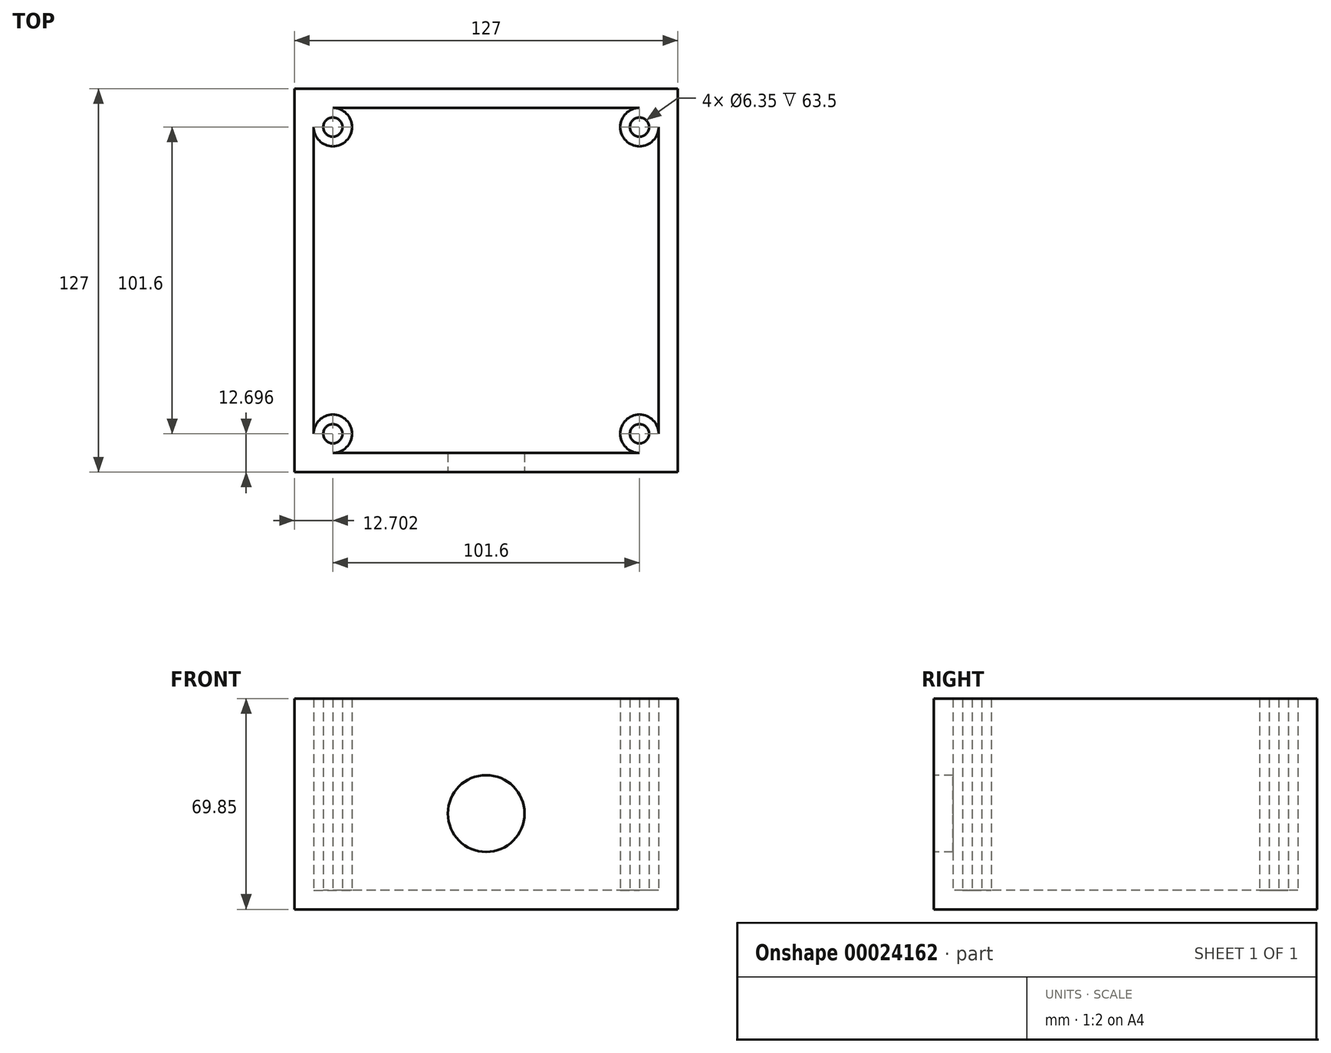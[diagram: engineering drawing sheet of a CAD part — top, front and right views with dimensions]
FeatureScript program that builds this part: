
annotation { "Feature Type Name" : "Feature", "Feature Type Description" : "" }
export const myFeature = defineFeature(function(context is Context, id is Id, definition is map)
    precondition{}
    {
        {
            var Q0;
            Q0=qCreatedBy(makeId("Top.planeOp"),FACE);
            var sketch = newSketch(context, id + "F0", { "sketchPlane" : qUnion([Q0])});
            skLineSegment(sketch, "E0.bottom", {"start": v(-155.82, 63.15) * mm, "end": v(-28.82, 63.15) * mm});
            skLineSegment(sketch, "E0.top", {"start": v(-155.82, -63.85) * mm, "end": v(-28.82, -63.85) * mm});
            skLineSegment(sketch, "E0.left", {"start": v(-155.82, 63.15) * mm, "end": v(-155.82, -63.85) * mm});
            skLineSegment(sketch, "E0.right", {"start": v(-28.82, 63.15) * mm, "end": v(-28.82, -63.85) * mm});
            skSolve(sketch);
        }
        {
            var Q0;
            Q0=makeQuery(id+"F0.imprint","IMPRINT",FACE,{"disambiguationData":[TD([[makeQuery(id+"F0.imprint","IMPRINT",EDGE,{"derivedFrom":sQuery(id+"F0.wireOp",EDGE,"E0.bottom")}),-1.0]])]});
            extrude(context, id + "F1", {"entities" : qUnion([Q0]), "depth" : 6.35 * mm});
        }
        {
            var Q0;
            Q0=makeQuery(id+"F1.opExtrude","CAP_FACE",FACE,{"disambiguationData":[OSD([sQuery(id+"F0.wireOp",EDGE,"E0.bottom"),sQuery(id+"F0.wireOp",EDGE,"E0.top"),sQuery(id+"F0.wireOp",EDGE,"E0.left"),sQuery(id+"F0.wireOp",EDGE,"E0.right")])],"isStart":false});
            var sketch = newSketch(context, id + "F2", { "sketchPlane" : qUnion([Q0])});
            skLineSegment(sketch, "E1.bottom", {"start": v(-155.82, -63.85) * mm, "end": v(-149.47, -63.85) * mm});
            skLineSegment(sketch, "E1.top", {"start": v(-155.82, 63.15) * mm, "end": v(-149.47, 63.15) * mm});
            skLineSegment(sketch, "E1.left", {"start": v(-155.82, -63.85) * mm, "end": v(-155.82, 63.15) * mm});
            skLineSegment(sketch, "E1.right", {"start": v(-149.47, -63.85) * mm, "end": v(-149.47, 63.15) * mm});
            skLineSegment(sketch, "E2.bottom", {"start": v(-155.82, 63.15) * mm, "end": v(-28.82, 63.15) * mm});
            skLineSegment(sketch, "E2.top", {"start": v(-155.82, 56.8) * mm, "end": v(-28.82, 56.8) * mm});
            skLineSegment(sketch, "E2.left", {"start": v(-155.82, 63.15) * mm, "end": v(-155.82, 56.8) * mm});
            skLineSegment(sketch, "E2.right", {"start": v(-28.82, 63.15) * mm, "end": v(-28.82, 56.8) * mm});
            skLineSegment(sketch, "E3.bottom", {"start": v(-28.82, 63.15) * mm, "end": v(-35.17, 63.15) * mm});
            skLineSegment(sketch, "E3.top", {"start": v(-28.82, -63.85) * mm, "end": v(-35.17, -63.85) * mm});
            skLineSegment(sketch, "E3.left", {"start": v(-28.82, 63.15) * mm, "end": v(-28.82, -63.85) * mm});
            skLineSegment(sketch, "E3.right", {"start": v(-35.17, 63.15) * mm, "end": v(-35.17, -63.85) * mm});
            skLineSegment(sketch, "E4.bottom", {"start": v(-28.82, -63.85) * mm, "end": v(-155.82, -63.85) * mm});
            skLineSegment(sketch, "E4.top", {"start": v(-28.82, -57.5) * mm, "end": v(-155.82, -57.5) * mm});
            skLineSegment(sketch, "E4.left", {"start": v(-28.82, -63.85) * mm, "end": v(-28.82, -57.5) * mm});
            skLineSegment(sketch, "E4.right", {"start": v(-155.82, -63.85) * mm, "end": v(-155.82, -57.5) * mm});
            skSolve(sketch);
        }
        {
            var Q0;
            Q0 = qSketchRegion(id + "F2", true);
            extrude(context, id + "F3", {"entities" : qUnion([Q0]), "operationType" : NewBodyOperationType.ADD, "depth" : 63.5 * mm});
        }
        {
            var Q0;
            Q0=makeQuery(id+"F3.boolean.opBoolean","MERGE",FACE,{"derivedFrom":[makeQuery(id+"F1.opExtrude","SWEPT_FACE",FACE,{"disambiguationData":[OSD([sQuery(id+"F0.wireOp",EDGE,"E0.top")])]}),makeQuery(id+"F3.opExtrude","SWEPT_FACE",FACE,{"disambiguationData":[OSD([sQuery(id+"F2.wireOp",EDGE,"E4.bottom")])]})]});
            var sketch = newSketch(context, id + "F4", { "sketchPlane" : qUnion([Q0])});
            skCircle(sketch, "E5", {"center": v(-92.32, 31.75) * mm, "radius": 12.7 * mm});
            skSolve(sketch);
        }
        {
            var Q0;
            Q0 = qSketchRegion(id + "F4", true);
            extrude(context, id + "F5", {"entities" : qUnion([Q0]), "operationType" : NewBodyOperationType.REMOVE, "oppositeDirection" : true, "depth" : 25.4 * mm});
        }
        {
            var Q0;
            Q0=makeQuery(id+"F1.opExtrude","CAP_FACE",FACE,{"disambiguationData":[OSD([sQuery(id+"F0.wireOp",EDGE,"E0.bottom"),sQuery(id+"F0.wireOp",EDGE,"E0.top"),sQuery(id+"F0.wireOp",EDGE,"E0.left"),sQuery(id+"F0.wireOp",EDGE,"E0.right")])],"isStart":false});
            var sketch = newSketch(context, id + "F6", { "sketchPlane" : qUnion([Q0])});
            skCircle(sketch, "E6", {"center": v(-143.12, 50.45) * mm, "radius": 6.35 * mm});
            skCircle(sketch, "E7", {"center": v(-143.12, 50.45) * mm, "radius": 3.18 * mm});
            skSolve(sketch);
        }
        {
            var Q0;
            Q0 = qSketchRegion(id + "F6", true);
            var Q1;
            {var subQ1=sQuery(id+"F6.wireOp",EDGE,"E6");var subQ3=makeQuery(id+"F3.opExtrude","CAP_EDGE",EDGE,{"disambiguationData":[OSD([sQuery(id+"F2.wireOp",EDGE,"E1.right")])],"isStart":true});var subQ5=makeQuery(id+"F6.imprint","INTERSECT",VERTEX,{"derivedFrom":[subQ3,subQ1]});Q1=makeQuery(id+"F6.imprint","IMPRINT",FACE,{"disambiguationData":[TD([[makeQuery(id+"F6.imprint","IMPRINT",EDGE,{"disambiguationData":[TD([[subQ5,1.0]])],"derivedFrom":subQ1}),-1.0]])]});}
            extrude(context, id + "F7", {"entities" : qUnion([Q0, Q1]), "operationType" : NewBodyOperationType.ADD, "depth" : 63.5 * mm});
        }
        {
            var Q0;
            Q0=makeQuery(id+"F7.boolean.opBoolean","SPLIT",FACE,{"disambiguationData":[TD([makeQuery(id+"F3.opExtrude","SWEPT_FACE",FACE,{"disambiguationData":[OSD([sQuery(id+"F2.wireOp",EDGE,"E1.right")])]})])],"derivedFrom":makeQuery(id+"F1.opExtrude","CAP_FACE",FACE,{"disambiguationData":[OSD([sQuery(id+"F0.wireOp",EDGE,"E0.bottom"),sQuery(id+"F0.wireOp",EDGE,"E0.top"),sQuery(id+"F0.wireOp",EDGE,"E0.left"),sQuery(id+"F0.wireOp",EDGE,"E0.right")])],"isStart":false})});
            var sketch = newSketch(context, id + "F8", { "sketchPlane" : qUnion([Q0])});
            skCircle(sketch, "E8", {"center": v(-41.52, 50.45) * mm, "radius": 3.18 * mm});
            skCircle(sketch, "E9", {"center": v(-41.52, 50.45) * mm, "radius": 6.35 * mm});
            skSolve(sketch);
        }
        {
            var Q0;
            Q0=makeQuery(id+"F8.imprint","IMPRINT",FACE,{"disambiguationData":[TD([[makeQuery(id+"F8.imprint","IMPRINT",EDGE,{"derivedFrom":sQuery(id+"F8.wireOp",EDGE,"E8")}),-1.0]])]});
            var Q1;
            {var subQ1=sQuery(id+"F8.wireOp",EDGE,"E9");var subQ3=makeQuery(id+"F3.opExtrude","CAP_EDGE",EDGE,{"disambiguationData":[OSD([sQuery(id+"F2.wireOp",EDGE,"E3.right")])],"isStart":true});var subQ5=makeQuery(id+"F8.imprint","INTERSECT",VERTEX,{"derivedFrom":[subQ3,subQ1]});Q1=makeQuery(id+"F8.imprint","IMPRINT",FACE,{"disambiguationData":[TD([[makeQuery(id+"F8.imprint","IMPRINT",EDGE,{"disambiguationData":[TD([[subQ5,-1.0]])],"derivedFrom":subQ1}),-1.0]])]});}
            extrude(context, id + "F9", {"entities" : qUnion([Q0, Q1]), "operationType" : NewBodyOperationType.ADD, "depth" : 63.5 * mm});
        }
        {
            var Q0;
            {var subQ4=makeQuery(id+"F3.opExtrude","SWEPT_FACE",FACE,{"disambiguationData":[OSD([sQuery(id+"F2.wireOp",EDGE,"E1.right")])]});Q0=makeQuery(id+"F9.boolean.opBoolean","SPLIT",FACE,{"disambiguationData":[TD([subQ4])],"derivedFrom":makeQuery(id+"F7.boolean.opBoolean","SPLIT",FACE,{"disambiguationData":[TD([subQ4])],"derivedFrom":makeQuery(id+"F1.opExtrude","CAP_FACE",FACE,{"disambiguationData":[OSD([sQuery(id+"F0.wireOp",EDGE,"E0.bottom"),sQuery(id+"F0.wireOp",EDGE,"E0.top"),sQuery(id+"F0.wireOp",EDGE,"E0.left"),sQuery(id+"F0.wireOp",EDGE,"E0.right")])],"isStart":false})})});}
            var sketch = newSketch(context, id + "F10", { "sketchPlane" : qUnion([Q0])});
            skCircle(sketch, "E10", {"center": v(-143.12, -51.15) * mm, "radius": 6.35 * mm});
            skCircle(sketch, "E11", {"center": v(-143.12, -51.15) * mm, "radius": 3.18 * mm});
            skCircle(sketch, "E12", {"center": v(-41.52, -51.15) * mm, "radius": 6.35 * mm});
            skCircle(sketch, "E13", {"center": v(-41.52, -51.15) * mm, "radius": 3.18 * mm});
            skSolve(sketch);
        }
        {
            var Q0;
            Q0=makeQuery(id+"F10.imprint","IMPRINT",FACE,{"disambiguationData":[TD([[makeQuery(id+"F10.imprint","IMPRINT",EDGE,{"derivedFrom":sQuery(id+"F10.wireOp",EDGE,"E11")}),-1.0]])]});
            var Q1;
            {var subQ1=sQuery(id+"F10.wireOp",EDGE,"E10");var subQ3=makeQuery(id+"F3.opExtrude","CAP_EDGE",EDGE,{"disambiguationData":[OSD([sQuery(id+"F2.wireOp",EDGE,"E4.top")])],"isStart":true});var subQ5=makeQuery(id+"F10.imprint","INTERSECT",VERTEX,{"derivedFrom":[subQ3,subQ1]});Q1=makeQuery(id+"F10.imprint","IMPRINT",FACE,{"disambiguationData":[TD([[makeQuery(id+"F10.imprint","IMPRINT",EDGE,{"disambiguationData":[TD([[subQ5,1.0]])],"derivedFrom":subQ1}),-1.0]])]});}
            var Q2;
            Q2=makeQuery(id+"F10.imprint","IMPRINT",FACE,{"disambiguationData":[TD([[makeQuery(id+"F10.imprint","IMPRINT",EDGE,{"derivedFrom":sQuery(id+"F10.wireOp",EDGE,"E13")}),-1.0]])]});
            var Q3;
            {var subQ1=sQuery(id+"F10.wireOp",EDGE,"E12");var subQ3=makeQuery(id+"F3.opExtrude","CAP_EDGE",EDGE,{"disambiguationData":[OSD([sQuery(id+"F2.wireOp",EDGE,"E4.top")])],"isStart":true});var subQ5=makeQuery(id+"F10.imprint","INTERSECT",VERTEX,{"derivedFrom":[subQ3,subQ1]});Q3=makeQuery(id+"F10.imprint","IMPRINT",FACE,{"disambiguationData":[TD([[makeQuery(id+"F10.imprint","IMPRINT",EDGE,{"disambiguationData":[TD([[subQ5,-1.0]])],"derivedFrom":subQ1}),-1.0]])]});}
            extrude(context, id + "F11", {"entities" : qUnion([Q0, Q1, Q2, Q3]), "operationType" : NewBodyOperationType.ADD, "depth" : 63.5 * mm});
        }
    });
